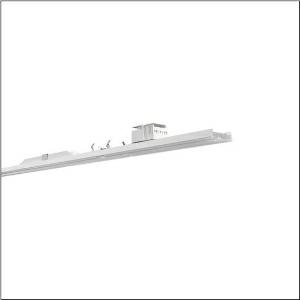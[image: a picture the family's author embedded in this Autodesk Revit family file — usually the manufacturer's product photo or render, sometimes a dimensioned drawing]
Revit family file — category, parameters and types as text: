
# Revit family: licross_r__11_recessed_extreme_mo_51tl12dn49xfe_b4ac
name_source: partatom
category: Lighting Fixtures
units: mm (PartAtom-declared; Revit-internal decimal feet)

## family parameters
Cut with Voids When Loaded = No
Host = Face
Light Source = No
Part Type = Normal
Room Calculation Point = No
Round Connector Dimension = Use Diameter
Shared = No

## types (1)
- --- (1 x LED, 9140 lm, 55.4 W, 4000K)
    Apparent Load = 55 VA
    CIE Flux Codes = 67 92 99 100 100
    Color Rendering = 80
    Color Temperature = 4000K
    Default Elevation = 1800 mm
    Description = Licross® 11 Recessed extreme MOluminaire insert, length: 1.500mm, width: 66mm, height: 67mm, LED rated luminous flux: 9.140lm, light colour: 840, control gear: DALI 2, control gear: ECG DALI, with plug, 5-pole, with phase selection, mains connection: 220..240V, AC, 50/60Hz, halogen-free wiring, primary optical cover: cover, of PMMA, light emission: direct distribution, protection rating (complete): IP40, insulation class (complete): insulation class I (protective earthing), certification: CE, ENEC, VDE, protection symbol: D if used in an environment without relevant dust loads with corresponding accessories, permissible ambient temperature for indoor applications: -25..+50°C, reducing of maximum allowable ambient temperature of 5°C with ceiling mounting, corresponds to IFS (International Featured Standards) requirements for safety and quality in the food industry, packaging unit: 1 piece
    Height = 58 mm
    Lamp = 1 x LED
    Lamp Light Flux = 9140 lm
    Lamp Power = 55.4 W
    Lamp count = 1
    Length = 1500 mm
    Luminous efficacy = 165 lm/W
    Manufacturer = Siteco
    ModVariant = No
    Model = 51TL12DN49XFE
    Mounting Place = Ceiling
    Mounting Type = Pendant
    Number of Poles = 1
    OnlyDefault = Yes
    Power Factor = 1
    Product Name = Licross® 11 Recessed extreme MO
    Product group = luminaire insert
    ProductGroupID = 902
    Protection Class = Protection class I
    Protection Degree = IP 40
    RLX_Detail_Level = 1
    RlxData = <blob elided: 22125 chars, md5=a9696f54>
    Socket = socket
    Standby Power = 0 W
    System Light Flux = 9140 lm
    System Power = 55 W
    Type Comments = factory setting: luminous flux: 100 % | dim-lin: 254 | 365 mA
    Type Image = l_1266722.jpg
    URL = http://relux.com
    VarID = @adj_132634
    Voltage = 0 V
    Weight = 0.00 kg
    Width = 66 mm

## geometry (parser evidence)
native form markers: Blend x4, Sweep x11
no freeform markers — native parametric forms only
